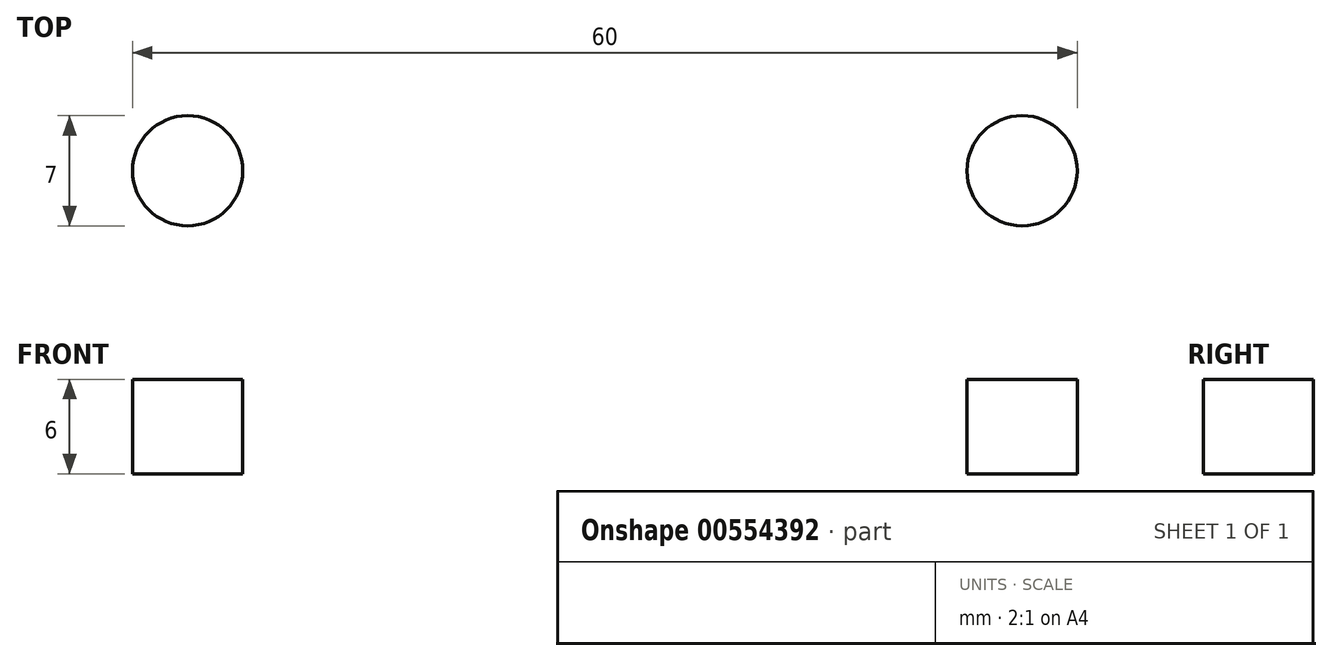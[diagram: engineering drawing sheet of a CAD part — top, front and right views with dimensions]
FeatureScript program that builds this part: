
annotation { "Feature Type Name" : "Feature", "Feature Type Description" : "" }
export const myFeature = defineFeature(function(context is Context, id is Id, definition is map)
    precondition{}
    {
        {
            var Q0;
            Q0=qCreatedBy(makeId("Front.planeOp"),FACE);
            var sketch = newSketch(context, id + "F0", { "sketchPlane" : qUnion([Q0])});
            skArc(sketch, "E0", {"start": v(-0.87, 0) * mm, "mid": v(0, -0.02) * mm, "end": v(0.85, 0) * mm});
            skLineSegment(sketch, "E1", {"start": v(0, 0) * mm, "end": v(33.5, 0) * mm});
            skLineSegment(sketch, "E2", {"start": v(33.5, 0) * mm, "end": v(33.5, 6) * mm});
            skLineSegment(sketch, "E3", {"start": v(17.48, 18.12) * mm, "end": v(17.48, 6) * mm});
            skLineSegment(sketch, "E4", {"start": v(33.5, 6) * mm, "end": v(17.48, 6) * mm});
            skLineSegment(sketch, "E5.MirrorCS", {"start": v(-17.48, 18.12) * mm, "end": v(-17.48, 6) * mm});
            skLineSegment(sketch, "E6.MirrorCS", {"start": v(-33.5, 6) * mm, "end": v(-17.48, 6) * mm});
            skLineSegment(sketch, "E7.MirrorCS", {"start": v(-33.5, 0) * mm, "end": v(-33.5, 6) * mm});
            skLineSegment(sketch, "E8.MirrorCS", {"start": v(0, 0) * mm, "end": v(-33.5, 0) * mm});
            skArc(sketch, "E9.trimOffspring", {"start": v(17.48, 16.84) * mm, "mid": v(-0.17, 34.98) * mm, "end": v(-17.48, 16.52) * mm});
            skSolve(sketch);
        }
        {
            var Q0;
            {var subQ14=sQuery(id+"F0.wireOp",EDGE,"E2");Q0=makeQuery(id+"F0.imprint","IMPRINT",FACE,{"disambiguationData":[TD([[makeQuery(id+"F0.imprint","IMPRINT",EDGE,{"derivedFrom":subQ14}),1.0]])]});}
            extrude(context, id + "F1", {"entities" : qUnion([Q0]), "depth" : 14.5 * mm, "offsetDistance" : 25 * mm});
        }
        {
            var Q0;
            Q0=makeQuery(id+"F1.opExtrude","CAP_FACE",FACE,{"disambiguationData":[OSD([sQuery(id+"F0.wireOp",EDGE,"E1"),sQuery(id+"F0.wireOp",EDGE,"E2"),sQuery(id+"F0.wireOp",EDGE,"E3"),sQuery(id+"F0.wireOp",EDGE,"E4"),sQuery(id+"F0.wireOp",EDGE,"E5.MirrorCS"),sQuery(id+"F0.wireOp",EDGE,"E6.MirrorCS"),sQuery(id+"F0.wireOp",EDGE,"E7.MirrorCS"),sQuery(id+"F0.wireOp",EDGE,"E8.MirrorCS"),sQuery(id+"F0.wireOp",EDGE,"E9.trimOffspring")])],"isStart":false});
            var sketch = newSketch(context, id + "F2", { "sketchPlane" : qUnion([Q0])});
            skLineSegment(sketch, "E10", {"start": v(0, 0) * mm, "end": v(0, 23.15) * mm});
            skPoint(sketch, "E10.endSnap0", {"position": v(0, 0) * mm});
            skCircle(sketch, "E11", {"center": v(0, 18) * mm, "radius": 5 * mm});
            skSolve(sketch);
        }
        {
            var Q0;
            {var subQ0=sQuery(id+"F2.wireOp",EDGE,"E11");var subQ1=sQuery(id+"F2.wireOp",EDGE,"E10");var subQ2=makeQuery(id+"F2.imprint","INTERSECT",VERTEX,{"disambiguationData":[OD(0.0)],"derivedFrom":[subQ1,subQ0]});Q0=makeQuery(id+"F2.imprint","IMPRINT",FACE,{"disambiguationData":[TD([[makeQuery(id+"F2.imprint","IMPRINT",EDGE,{"disambiguationData":[TD([[subQ2,-1.0]])],"derivedFrom":subQ1}),1.0]])]});}
            var Q1;
            {var subQ0=sQuery(id+"F2.wireOp",EDGE,"E11");var subQ1=sQuery(id+"F2.wireOp",EDGE,"E10");var subQ2=makeQuery(id+"F2.imprint","INTERSECT",VERTEX,{"disambiguationData":[OD(0.0)],"derivedFrom":[subQ1,subQ0]});Q1=makeQuery(id+"F2.imprint","IMPRINT",FACE,{"disambiguationData":[TD([[makeQuery(id+"F2.imprint","IMPRINT",EDGE,{"disambiguationData":[TD([[subQ2,-1.0]])],"derivedFrom":subQ1}),-1.0]])]});}
            extrude(context, id + "F3", {"entities" : qUnion([Q0, Q1]), "operationType" : NewBodyOperationType.REMOVE, "endBound" : BoundingType.UP_TO_NEXT, "oppositeDirection" : true, "depth" : 25 * mm, "offsetDistance" : 25 * mm});
        }
        {
            var Q0;
            Q0=makeQuery(id+"F1.opExtrude","SWEPT_EDGE",EDGE,{"disambiguationData":[OSD([sQuery(id+"F0.wireOp",EDGE,"E5.MirrorCS"),sQuery(id+"F0.wireOp",EDGE,"E6.MirrorCS")])]});
            var Q1;
            Q1=makeQuery(id+"F1.opExtrude","SWEPT_EDGE",EDGE,{"disambiguationData":[OSD([sQuery(id+"F0.wireOp",EDGE,"E3"),sQuery(id+"F0.wireOp",EDGE,"E4")])]});
            fillet(context, id + "F4", {"entities" : qUnion([Q0, Q1]), "radius" : 1 * mm, "tangentPropagation" : true, "allowEdgeOverflow" : false});
        }
        {
            var Q0;
            Q0=makeQuery(id+"F1.opExtrude","SWEPT_FACE",FACE,{"disambiguationData":[OSD([sQuery(id+"F0.wireOp",EDGE,"E1"),sQuery(id+"F0.wireOp",EDGE,"E8.MirrorCS")])]});
            var sketch = newSketch(context, id + "F5", { "sketchPlane" : qUnion([Q0])});
            skLineSegment(sketch, "E12", {"start": v(33.5, 7.25) * mm, "end": v(-16.04, 7.25) * mm});
            skLineSegment(sketch, "E13", {"start": v(0, 0) * mm, "end": v(0, 10.77) * mm});
            skCircle(sketch, "E14", {"center": v(26.5, 7.25) * mm, "radius": 3.5 * mm});
            skCircle(sketch, "E15.MirrorC", {"center": v(-26.5, 7.25) * mm, "radius": 3.5 * mm});
            skSolve(sketch);
        }
        {
            var Q0;
            {var subQ0=sQuery(id+"F5.wireOp",EDGE,"E14");var subQ1=sQuery(id+"F5.wireOp",EDGE,"E12");var subQ2=makeQuery(id+"F5.imprint","INTERSECT",VERTEX,{"disambiguationData":[OD(0.0)],"derivedFrom":[subQ1,subQ0]});Q0=makeQuery(id+"F5.imprint","IMPRINT",FACE,{"disambiguationData":[TD([[makeQuery(id+"F5.imprint","IMPRINT",EDGE,{"disambiguationData":[TD([[subQ2,-1.0]])],"derivedFrom":subQ1}),-1.0]])]});}
            var Q1;
            {var subQ0=sQuery(id+"F5.wireOp",EDGE,"E14");var subQ1=sQuery(id+"F5.wireOp",EDGE,"E12");var subQ2=makeQuery(id+"F5.imprint","INTERSECT",VERTEX,{"disambiguationData":[OD(0.0)],"derivedFrom":[subQ1,subQ0]});Q1=makeQuery(id+"F5.imprint","IMPRINT",FACE,{"disambiguationData":[TD([[makeQuery(id+"F5.imprint","IMPRINT",EDGE,{"disambiguationData":[TD([[subQ2,-1.0]])],"derivedFrom":subQ1}),1.0]])]});}
            var Q2;
            Q2=makeQuery(id+"F5.imprint","IMPRINT",FACE,{"disambiguationData":[TD([[makeQuery(id+"F5.imprint","IMPRINT",EDGE,{"derivedFrom":sQuery(id+"F5.wireOp",EDGE,"E15.MirrorC")}),-1.0]])]});
            extrude(context, id + "F6", {"entities" : qUnion([Q0, Q1, Q2]), "operationType" : NewBodyOperationType.REMOVE, "endBound" : BoundingType.UP_TO_NEXT, "oppositeDirection" : true, "depth" : 25 * mm, "offsetDistance" : 25 * mm});
        }
    });
